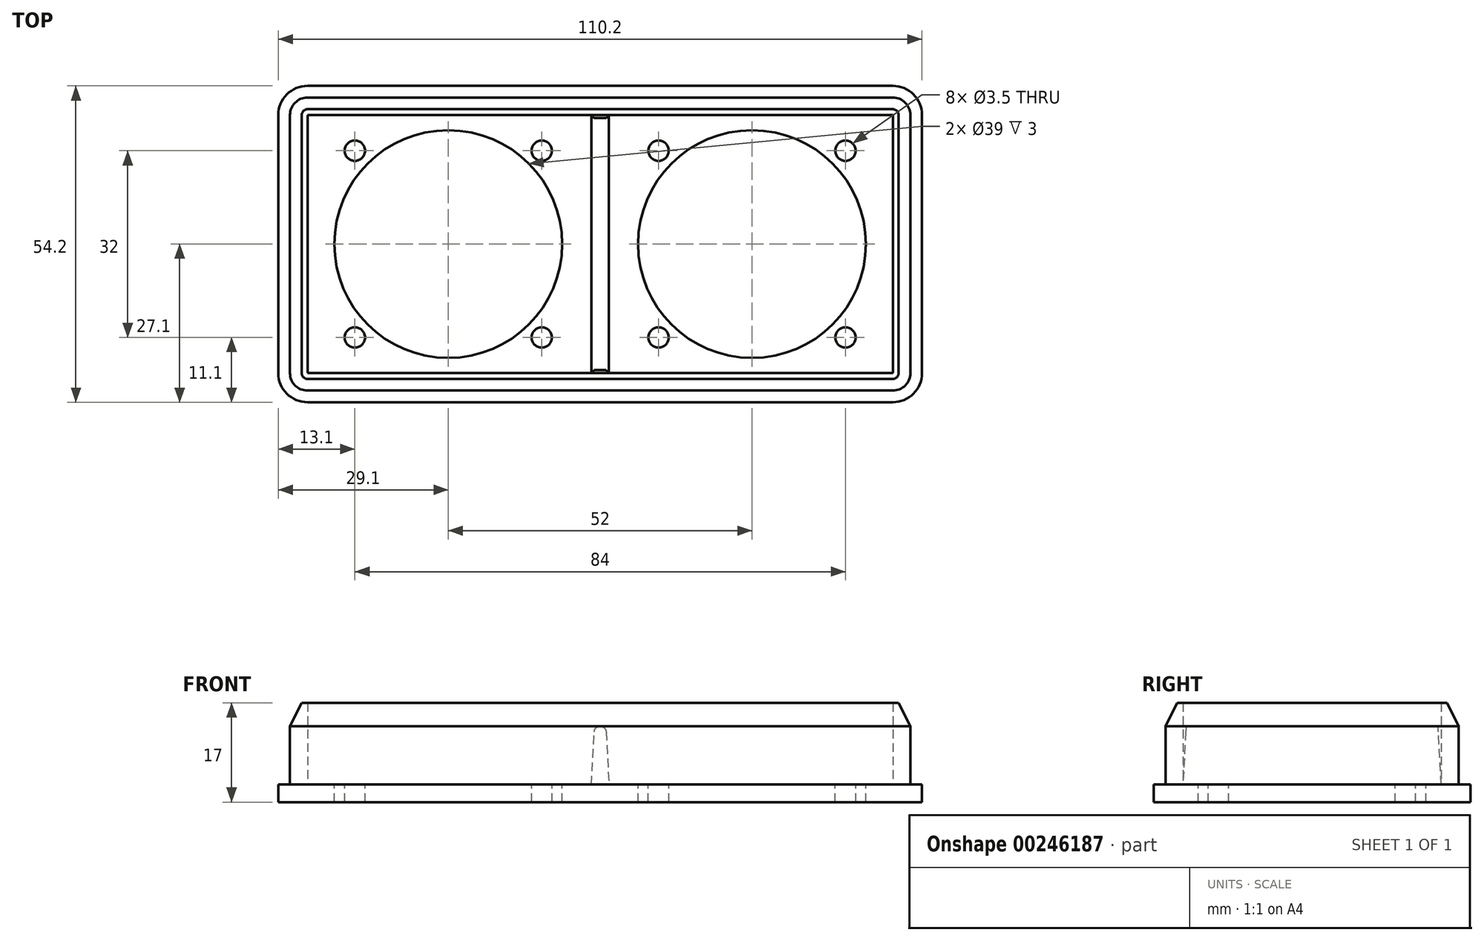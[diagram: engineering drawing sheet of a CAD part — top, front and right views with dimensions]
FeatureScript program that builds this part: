
annotation { "Feature Type Name" : "Feature", "Feature Type Description" : "" }
export const myFeature = defineFeature(function(context is Context, id is Id, definition is map)
    precondition{}
    {
        {
            var Q0;
            Q0=qCreatedBy(makeId("Top.planeOp"),FACE);
            var sketch = newSketch(context, id + "F0", { "sketchPlane" : qUnion([Q0])});
            skLineSegment(sketch, "E0.bottom", {"start": v(5, 0) * mm, "end": v(105.2, 0) * mm});
            skLineSegment(sketch, "E0.top", {"start": v(5, 54.2) * mm, "end": v(105.2, 54.2) * mm});
            skLineSegment(sketch, "E0.left", {"start": v(0, 5) * mm, "end": v(0, 49.2) * mm});
            skLineSegment(sketch, "E0.right", {"start": v(110.2, 5) * mm, "end": v(110.2, 49.2) * mm});
            skPoint(sketch, "E1.visualSharp", {"position": v(0, 54.2) * mm});
            skArc(sketch, "E1.filletArc", {"start": v(5, 54.2) * mm, "mid": v(1.46, 52.74) * mm, "end": v(0, 49.2) * mm});
            skPoint(sketch, "E2.visualSharp", {"position": v(110.2, 54.2) * mm});
            skArc(sketch, "E2.filletArc", {"start": v(110.2, 49.2) * mm, "mid": v(108.74, 52.74) * mm, "end": v(105.2, 54.2) * mm});
            skPoint(sketch, "E3.visualSharp", {"position": v(110.2, 0) * mm});
            skArc(sketch, "E3.filletArc", {"start": v(105.2, 0) * mm, "mid": v(108.74, 1.46) * mm, "end": v(110.2, 5) * mm});
            skPoint(sketch, "E4.visualSharp", {"position": v(0, 0) * mm});
            skArc(sketch, "E4.filletArc", {"start": v(0, 5) * mm, "mid": v(1.46, 1.46) * mm, "end": v(5, 0) * mm});
            skSolve(sketch);
        }
        {
            var Q0;
            Q0 = qSketchRegion(id + "F0", true);
            extrude(context, id + "F1", {"entities" : qUnion([Q0]), "depth" : 3 * mm});
        }
        {
            var Q0;
            Q0=makeQuery(id+"F1.opExtrude","CAP_FACE",FACE,{"disambiguationData":[OSD([sQuery(id+"F0.wireOp",EDGE,"E0.bottom"),sQuery(id+"F0.wireOp",EDGE,"E0.top"),sQuery(id+"F0.wireOp",EDGE,"E0.left"),sQuery(id+"F0.wireOp",EDGE,"E0.right"),sQuery(id+"F0.wireOp",EDGE,"E1.filletArc"),sQuery(id+"F0.wireOp",EDGE,"E2.filletArc"),sQuery(id+"F0.wireOp",EDGE,"E3.filletArc"),sQuery(id+"F0.wireOp",EDGE,"E4.filletArc")])],"isStart":false});
            var sketch = newSketch(context, id + "F2", { "sketchPlane" : qUnion([Q0])});
            skLineSegment(sketch, "E5.bottom", {"start": v(5, 2) * mm, "end": v(105.2, 2) * mm});
            skLineSegment(sketch, "E5.top", {"start": v(5, 52.2) * mm, "end": v(105.2, 52.2) * mm});
            skLineSegment(sketch, "E5.left", {"start": v(2, 5) * mm, "end": v(2, 49.2) * mm});
            skLineSegment(sketch, "E5.right", {"start": v(108.2, 5) * mm, "end": v(108.2, 49.2) * mm});
            skPoint(sketch, "E6.visualSharp", {"position": v(2, 52.2) * mm});
            skArc(sketch, "E6.filletArc", {"start": v(5, 52.2) * mm, "mid": v(2.88, 51.32) * mm, "end": v(2, 49.2) * mm});
            skPoint(sketch, "E7.visualSharp", {"position": v(108.2, 52.2) * mm});
            skArc(sketch, "E7.filletArc", {"start": v(108.2, 49.2) * mm, "mid": v(107.32, 51.32) * mm, "end": v(105.2, 52.2) * mm});
            skPoint(sketch, "E8.visualSharp", {"position": v(108.2, 2) * mm});
            skArc(sketch, "E8.filletArc", {"start": v(105.2, 2) * mm, "mid": v(107.32, 2.88) * mm, "end": v(108.2, 5) * mm});
            skPoint(sketch, "E9.visualSharp", {"position": v(2, 2) * mm});
            skArc(sketch, "E9.filletArc", {"start": v(2, 5) * mm, "mid": v(2.88, 2.88) * mm, "end": v(5, 2) * mm});
            skLineSegment(sketch, "E10.0", {"start": v(5, 5) * mm, "end": v(5, 49.2) * mm});
            skLineSegment(sketch, "E10.1", {"start": v(5, 5) * mm, "end": v(105.2, 5) * mm});
            skLineSegment(sketch, "E10.2", {"start": v(105.2, 5) * mm, "end": v(105.2, 49.2) * mm});
            skLineSegment(sketch, "E10.3", {"start": v(5, 49.2) * mm, "end": v(105.2, 49.2) * mm});
            skSolve(sketch);
        }
        {
            var Q0;
            Q0 = qSketchRegion(id + "F2", true);
            extrude(context, id + "F3", {"entities" : qUnion([Q0]), "operationType" : NewBodyOperationType.ADD, "depth" : 14 * mm});
        }
        {
            var Q0;
            Q0=makeQuery(id+"F3.opExtrude","CAP_EDGE",EDGE,{"disambiguationData":[OSD([sQuery(id+"F2.wireOp",EDGE,"E5.bottom")])],"isStart":false});
            chamfer(context, id + "F4", {"entities" : qUnion([Q0]), "chamferType" : ChamferType.TWO_OFFSETS, "width1" : 2 * mm, "oppositeDirection" : false, "width2" : 4 * mm, "tangentPropagation" : true});
        }
        {
            var Q0;
            Q0=makeQuery(id+"F3.boolean.opBoolean","SPLIT",FACE,{"disambiguationData":[TD([makeQuery(id+"F3.opExtrude","SWEPT_FACE",FACE,{"disambiguationData":[OSD([sQuery(id+"F2.wireOp",EDGE,"E10.0")])]})])],"derivedFrom":makeQuery(id+"F1.opExtrude","CAP_FACE",FACE,{"disambiguationData":[OSD([sQuery(id+"F0.wireOp",EDGE,"E0.bottom"),sQuery(id+"F0.wireOp",EDGE,"E0.top"),sQuery(id+"F0.wireOp",EDGE,"E0.left"),sQuery(id+"F0.wireOp",EDGE,"E0.right"),sQuery(id+"F0.wireOp",EDGE,"E1.filletArc"),sQuery(id+"F0.wireOp",EDGE,"E2.filletArc"),sQuery(id+"F0.wireOp",EDGE,"E3.filletArc"),sQuery(id+"F0.wireOp",EDGE,"E4.filletArc")])],"isStart":false})});
            var sketch = newSketch(context, id + "F5", { "sketchPlane" : qUnion([Q0])});
            skLineSegment(sketch, "E11", {"start": v(5, 27.1) * mm, "end": v(105.2, 27.1) * mm, "construction": true});
            skCircle(sketch, "E12", {"center": v(29.1, 27.1) * mm, "radius": 19.5 * mm});
            skLineSegment(sketch, "E13", {"start": v(55.1, 49.2) * mm, "end": v(55.1, 5) * mm, "construction": true});
            skCircle(sketch, "E14", {"center": v(13.1, 43.1) * mm, "radius": 1.75 * mm});
            skCircle(sketch, "E15.1.0", {"center": v(13.1, 11.1) * mm, "radius": 1.75 * mm});
            skCircle(sketch, "E15.2.0", {"center": v(45.1, 11.1) * mm, "radius": 1.75 * mm});
            skCircle(sketch, "E15.3.0", {"center": v(45.1, 43.1) * mm, "radius": 1.75 * mm});
            skCircle(sketch, "E16.MirrorC", {"center": v(81.1, 27.1) * mm, "radius": 19.5 * mm});
            skCircle(sketch, "E17.MirrorC", {"center": v(65.1, 43.1) * mm, "radius": 1.75 * mm});
            skCircle(sketch, "E18.MirrorC", {"center": v(65.1, 11.1) * mm, "radius": 1.75 * mm});
            skCircle(sketch, "E19.MirrorC", {"center": v(97.1, 11.1) * mm, "radius": 1.75 * mm});
            skCircle(sketch, "E20.MirrorC", {"center": v(97.1, 43.1) * mm, "radius": 1.75 * mm});
            skSolve(sketch);
        }
        {
            var Q0;
            Q0 = qSketchRegion(id + "F5", true);
            extrude(context, id + "F6", {"entities" : qUnion([Q0]), "operationType" : NewBodyOperationType.REMOVE, "endBound" : BoundingType.THROUGH_ALL, "oppositeDirection" : true, "depth" : 25 * mm});
        }
        {
            var Q0;
            Q0=makeQuery(id+"F3.boolean.opBoolean","SPLIT",FACE,{"disambiguationData":[TD([makeQuery(id+"F3.opExtrude","SWEPT_FACE",FACE,{"disambiguationData":[OSD([sQuery(id+"F2.wireOp",EDGE,"E10.0")])]})])],"derivedFrom":makeQuery(id+"F1.opExtrude","CAP_FACE",FACE,{"disambiguationData":[OSD([sQuery(id+"F0.wireOp",EDGE,"E0.bottom"),sQuery(id+"F0.wireOp",EDGE,"E0.top"),sQuery(id+"F0.wireOp",EDGE,"E0.left"),sQuery(id+"F0.wireOp",EDGE,"E0.right"),sQuery(id+"F0.wireOp",EDGE,"E1.filletArc"),sQuery(id+"F0.wireOp",EDGE,"E2.filletArc"),sQuery(id+"F0.wireOp",EDGE,"E3.filletArc"),sQuery(id+"F0.wireOp",EDGE,"E4.filletArc")])],"isStart":false})});
            var sketch = newSketch(context, id + "F7", { "sketchPlane" : qUnion([Q0])});
            skLineSegment(sketch, "E21", {"start": v(55.1, 49.2) * mm, "end": v(55.1, 5) * mm, "construction": true});
            skLineSegment(sketch, "E22.bottom", {"start": v(53.6, 49.2) * mm, "end": v(56.6, 49.2) * mm});
            skLineSegment(sketch, "E22.top", {"start": v(53.6, 5) * mm, "end": v(56.6, 5) * mm});
            skLineSegment(sketch, "E22.left", {"start": v(53.6, 49.2) * mm, "end": v(53.6, 5) * mm});
            skLineSegment(sketch, "E22.right", {"start": v(56.6, 49.2) * mm, "end": v(56.6, 5) * mm});
            skSolve(sketch);
        }
        {
            var Q0;
            Q0 = qSketchRegion(id + "F7", true);
            extrude(context, id + "F8", {"entities" : qUnion([Q0]), "operationType" : NewBodyOperationType.ADD, "depth" : 10 * mm, "hasDraft" : true, "draftAngle" : 3 * degree, "draftPullDirection" : true});
        }
        {
            var Q0;
            Q0=makeQuery(id+"F8.opExtrude","CAP_EDGE",EDGE,{"disambiguationData":[OSD([sQuery(id+"F7.wireOp",EDGE,"E22.right")])],"isStart":false});
            var Q1;
            Q1=makeQuery(id+"F8.opExtrude","CAP_EDGE",EDGE,{"disambiguationData":[OSD([sQuery(id+"F7.wireOp",EDGE,"E22.left")])],"isStart":false});
            fillet(context, id + "F9", {"entities" : qUnion([Q0, Q1]), "radius" : 1 * mm, "tangentPropagation" : true, "allowEdgeOverflow" : false});
        }
    });
